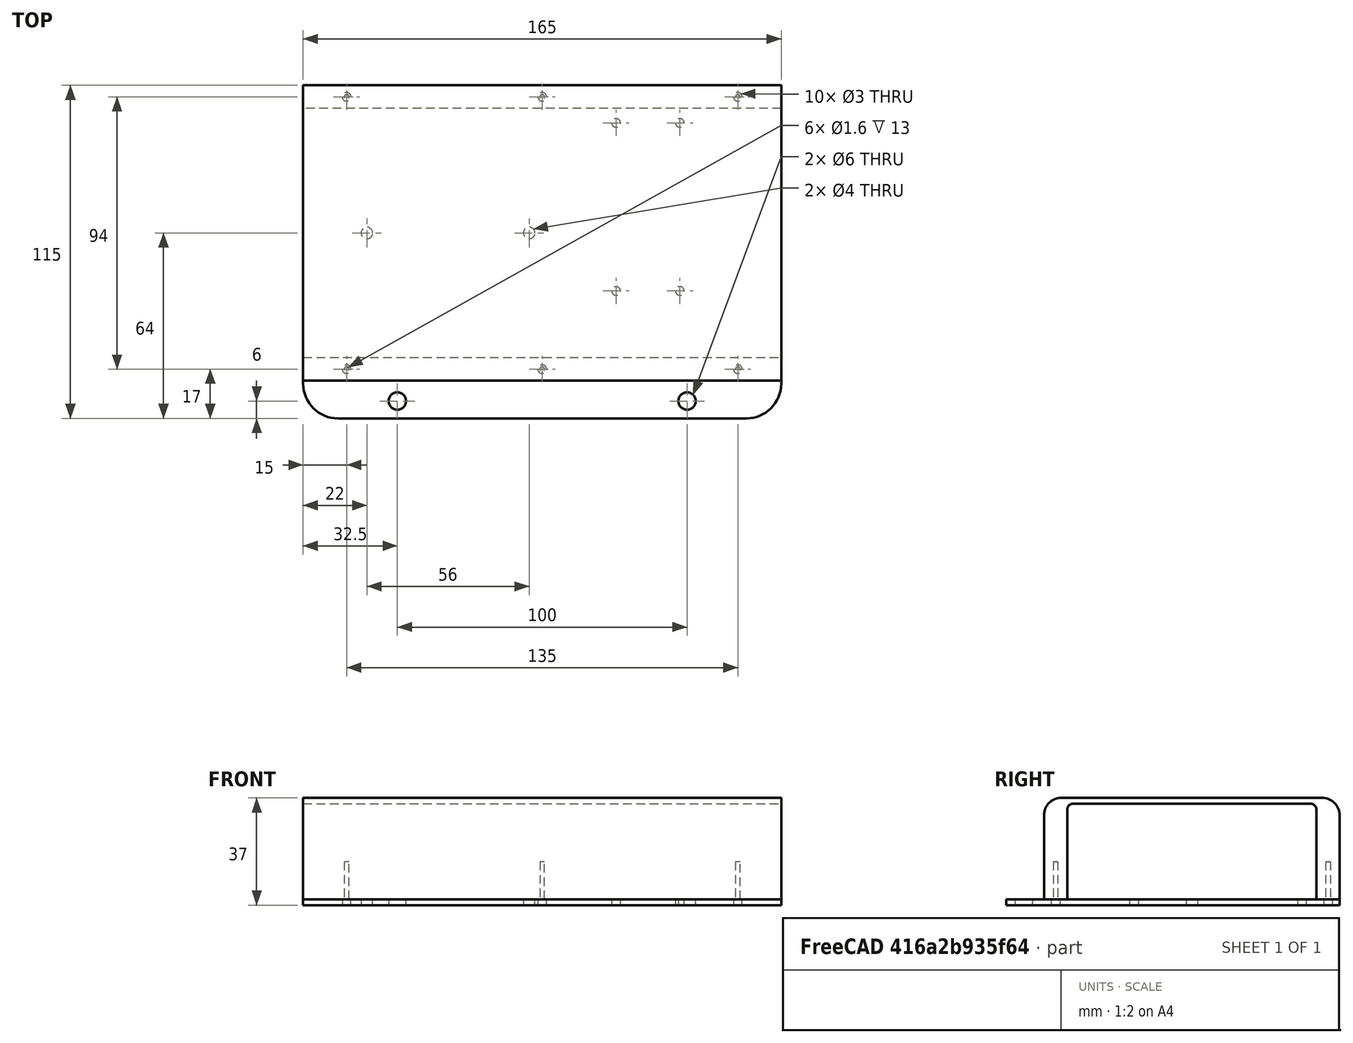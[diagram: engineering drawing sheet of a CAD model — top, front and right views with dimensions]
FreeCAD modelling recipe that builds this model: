
FCSTD DOCUMENT  (FreeCAD 1.0R39109 (Git))
Label: ReklamaKutija2
License: All rights reserved
LicenseURL: https://en.wikipedia.org/wiki/All_rights_reserved
objects: Part::Cylinder×20, Part::Box×3, Part::Fillet×3, Part::Cut×3, Part::MultiFuse×2
note: 31 computed .brp shape members not serialized (recipe doc carries the construction recipe); baked Part::Feature solids carry a one-line shape summary decoded from their .brp

FEATURE [Part::Cylinder] Cylinder  label="PwrScrew001"
  Angle = 360
  AttacherType = Attacher::AttachEngine3D
  FirstAngle = 0
  Height = 10
  Placement = pos=(28,0,0) rot=(0,0,1;0rad)
  Radius = 2
  SecondAngle = 0
FEATURE [Part::Cylinder] Cylinder001  label="PwrScrew002"
  Angle = 360
  AttacherType = Attacher::AttachEngine3D
  FirstAngle = 0
  Height = 10
  Placement = pos=(-28,0,0) rot=(0,0,1;0rad)
  Radius = 2
  SecondAngle = 0
FEATURE [Part::Box] Box  label="Base"
  AttacherType = Attacher::AttachEngine3D
  Height = 2
  Length = 165
  Placement = pos=(-50,-64,0) rot=(0,0,1;0rad)
  Width = 115
FEATURE [Part::Cylinder] Cylinder002  label="ComputerScrew001"
  Angle = 360
  AttacherType = Attacher::AttachEngine3D
  FirstAngle = 0
  Height = 10
  Placement = pos=(58,38,0) rot=(0,0,1;0rad)
  Radius = 1.5
  SecondAngle = 0
FEATURE [Part::Cylinder] Cylinder003  label="ComputerScrew002"
  Angle = 360
  AttacherType = Attacher::AttachEngine3D
  FirstAngle = 0
  Height = 10
  Placement = pos=(58,-20,0) rot=(0,0,1;0rad)
  Radius = 1.5
  SecondAngle = 0
FEATURE [Part::Cylinder] Cylinder004  label="ComputerScrew003"
  Angle = 360
  AttacherType = Attacher::AttachEngine3D
  FirstAngle = 0
  Height = 10
  Placement = pos=(80,38,0) rot=(0,0,1;0rad)
  Radius = 1.5
  SecondAngle = 0
FEATURE [Part::Cylinder] Cylinder005  label="ComputerScrew004"
  Angle = 360
  AttacherType = Attacher::AttachEngine3D
  FirstAngle = 0
  Height = 10
  Placement = pos=(80,-20,0) rot=(0,0,1;0rad)
  Radius = 1.5
  SecondAngle = 0
FEATURE [Part::Box] Box001  label="Hollow"
  AttacherType = Attacher::AttachEngine3D
  Height = 35
  Length = 165
  Placement = pos=(-50,-43,0) rot=(0,0,1;0rad)
  Width = 86
FEATURE [Part::Cylinder] Cylinder006  label="MainScrew001"
  Angle = 360
  AttacherType = Attacher::AttachEngine3D
  FirstAngle = 0
  Height = 10
  Placement = pos=(-17.5,-58,0) rot=(0,0,1;0rad)
  Radius = 3
  SecondAngle = 0
FEATURE [Part::Cylinder] Cylinder007  label="MainScrew002"
  Angle = 360
  AttacherType = Attacher::AttachEngine3D
  FirstAngle = 0
  Height = 10
  Placement = pos=(82.5,-58,0) rot=(0,0,1;0rad)
  Radius = 3
  SecondAngle = 0
FEATURE [Part::Fillet] Fillet
  Base = -> Box001
  EdgeLinks = -> Box001 [Edge10,Edge12]
  Edges = 2 edges r=2: [Edge10,Edge12]
FEATURE [Part::Box] Box002  label="Hollow001"
  AttacherType = Attacher::AttachEngine3D
  Height = 35
  Length = 165
  Placement = pos=(-50,-51,2) rot=(0,0,1;0rad)
  Width = 102
FEATURE [Part::Fillet] Fillet001
  Base = -> Box002
  EdgeLinks = -> Box002 [Edge10,Edge12]
  Edges = 2 edges r=6: [Edge10,Edge12]
FEATURE [Part::Cut] Cut
  Base = -> Fillet001
  Tool = -> Fillet
FEATURE [Part::Cylinder] Cylinder008  label="BoxScrew001"
  Angle = 360
  AttacherType = Attacher::AttachEngine3D
  FirstAngle = 0
  Height = 10
  Placement = pos=(100,47,0) rot=(0,0,1;0rad)
  Radius = 1.5
  SecondAngle = 0
FEATURE [Part::Cylinder] Cylinder009  label="BoxScrew002"
  Angle = 360
  AttacherType = Attacher::AttachEngine3D
  FirstAngle = 0
  Height = 10
  Placement = pos=(-35,47,0) rot=(0,0,1;0rad)
  Radius = 1.5
  SecondAngle = 0
FEATURE [Part::Cylinder] Cylinder010  label="BoxScrew003"
  Angle = 360
  AttacherType = Attacher::AttachEngine3D
  FirstAngle = 0
  Height = 10
  Placement = pos=(32.5,47,0) rot=(0,0,1;0rad)
  Radius = 1.5
  SecondAngle = 0
FEATURE [Part::Cylinder] Cylinder011  label="BoxScrew004"
  Angle = 360
  AttacherType = Attacher::AttachEngine3D
  FirstAngle = 0
  Height = 10
  Placement = pos=(100,-47,0) rot=(0,0,1;0rad)
  Radius = 1.5
  SecondAngle = 0
FEATURE [Part::Cylinder] Cylinder012  label="BoxScrew005"
  Angle = 360
  AttacherType = Attacher::AttachEngine3D
  FirstAngle = 0
  Height = 10
  Placement = pos=(-35,-47,0) rot=(0,0,1;0rad)
  Radius = 1.5
  SecondAngle = 0
FEATURE [Part::Cylinder] Cylinder013  label="BoxScrew006"
  Angle = 360
  AttacherType = Attacher::AttachEngine3D
  FirstAngle = 0
  Height = 10
  Placement = pos=(32.5,-47,0) rot=(0,0,1;0rad)
  Radius = 1.5
  SecondAngle = 0
FEATURE [Part::MultiFuse] Fusion  label="ScrewHolles"
  Shapes = -> [Cylinder,Cylinder001,Cylinder002,Cylinder003,Cylinder004,Cylinder005,Cylinder006,Cylinder007,Cylinder008,Cylinder009,Cylinder010,Cylinder011,Cylinder012,Cylinder013]
FEATURE [Part::Cut] Cut001  label="BaseSide"
  Base = -> Box
  Tool = -> Fusion
FEATURE [Part::Cylinder] Cylinder014  label="BoxScrew007"
  Angle = 360
  AttacherType = Attacher::AttachEngine3D
  FirstAngle = 0
  Height = 15
  Placement = pos=(100,47,0) rot=(0,0,1;0rad)
  Radius = 0.8
  SecondAngle = 0
FEATURE [Part::Cylinder] Cylinder015  label="BoxScrew008"
  Angle = 360
  AttacherType = Attacher::AttachEngine3D
  FirstAngle = 0
  Height = 15
  Placement = pos=(-35,47,0) rot=(0,0,1;0rad)
  Radius = 0.8
  SecondAngle = 0
FEATURE [Part::Cylinder] Cylinder016  label="BoxScrew009"
  Angle = 360
  AttacherType = Attacher::AttachEngine3D
  FirstAngle = 0
  Height = 15
  Placement = pos=(32.5,47,0) rot=(0,0,1;0rad)
  Radius = 0.8
  SecondAngle = 0
FEATURE [Part::Cylinder] Cylinder017  label="BoxScrew010"
  Angle = 360
  AttacherType = Attacher::AttachEngine3D
  FirstAngle = 0
  Height = 15
  Placement = pos=(100,-47,0) rot=(0,0,1;0rad)
  Radius = 0.8
  SecondAngle = 0
FEATURE [Part::Cylinder] Cylinder018  label="BoxScrew011"
  Angle = 360
  AttacherType = Attacher::AttachEngine3D
  FirstAngle = 0
  Height = 15
  Placement = pos=(-35,-47,0) rot=(0,0,1;0rad)
  Radius = 0.8
  SecondAngle = 0
FEATURE [Part::Cylinder] Cylinder019  label="BoxScrew012"
  Angle = 360
  AttacherType = Attacher::AttachEngine3D
  FirstAngle = 0
  Height = 15
  Placement = pos=(32.5,-47,0) rot=(0,0,1;0rad)
  Radius = 0.8
  SecondAngle = 0
FEATURE [Part::MultiFuse] Fusion001
  Shapes = -> [Cylinder019,Cylinder014,Cylinder015,Cylinder016,Cylinder017,Cylinder018]
FEATURE [Part::Cut] Cut002  label="Cover"
  Base = -> Cut
  Tool = -> Fusion001
FEATURE [Part::Fillet] Fillet002  label="Base001"
  Base = -> Cut001
  EdgeLinks = -> Cut001 [Edge1,Edge6]
  Edges = 2 edges r=12: [Edge1,Edge6]
